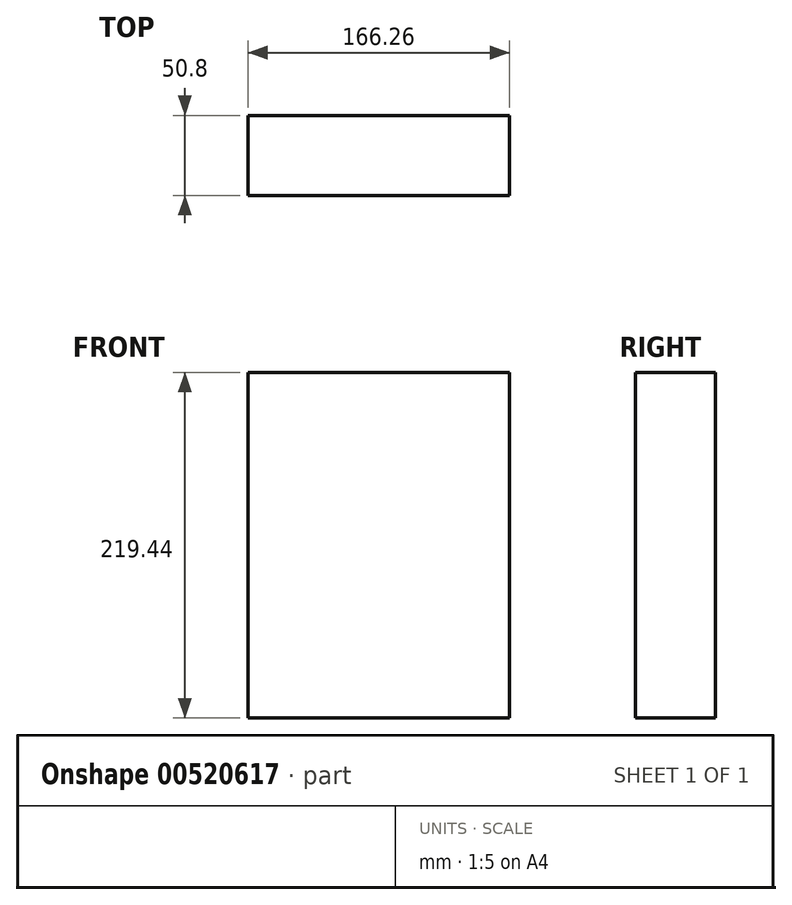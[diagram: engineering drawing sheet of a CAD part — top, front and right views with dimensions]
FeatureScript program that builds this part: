
annotation { "Feature Type Name" : "Feature", "Feature Type Description" : "" }
export const myFeature = defineFeature(function(context is Context, id is Id, definition is map)
    precondition{}
    {
        {
            var Q0;
            Q0=qCreatedBy(makeId("Front.planeOp"),FACE);
            var sketch = newSketch(context, id + "F0", { "sketchPlane" : qUnion([Q0])});
            skLineSegment(sketch, "E0.bottom", {"start": v(83.13, 109.72) * mm, "end": v(-83.13, 109.72) * mm});
            skLineSegment(sketch, "E0.top", {"start": v(83.13, -109.72) * mm, "end": v(-83.13, -109.72) * mm});
            skLineSegment(sketch, "E0.left", {"start": v(83.13, 109.72) * mm, "end": v(83.13, -109.72) * mm});
            skLineSegment(sketch, "E0.right", {"start": v(-83.13, 109.72) * mm, "end": v(-83.13, -109.72) * mm});
            skPoint(sketch, "E0.middle", {"position": v(0, 0) * mm});
            skSolve(sketch);
        }
        {
            var Q0;
            Q0=makeQuery(id+"F0.imprint","IMPRINT",FACE,{"disambiguationData":[TD([[makeQuery(id+"F0.imprint","IMPRINT",EDGE,{"derivedFrom":sQuery(id+"F0.wireOp",EDGE,"E0.bottom")}),1.0]])]});
            extrude(context, id + "F1", {"entities" : qUnion([Q0]), "depth" : 50.8 * mm, "offsetDistance" : 25.4 * mm});
        }
    });
